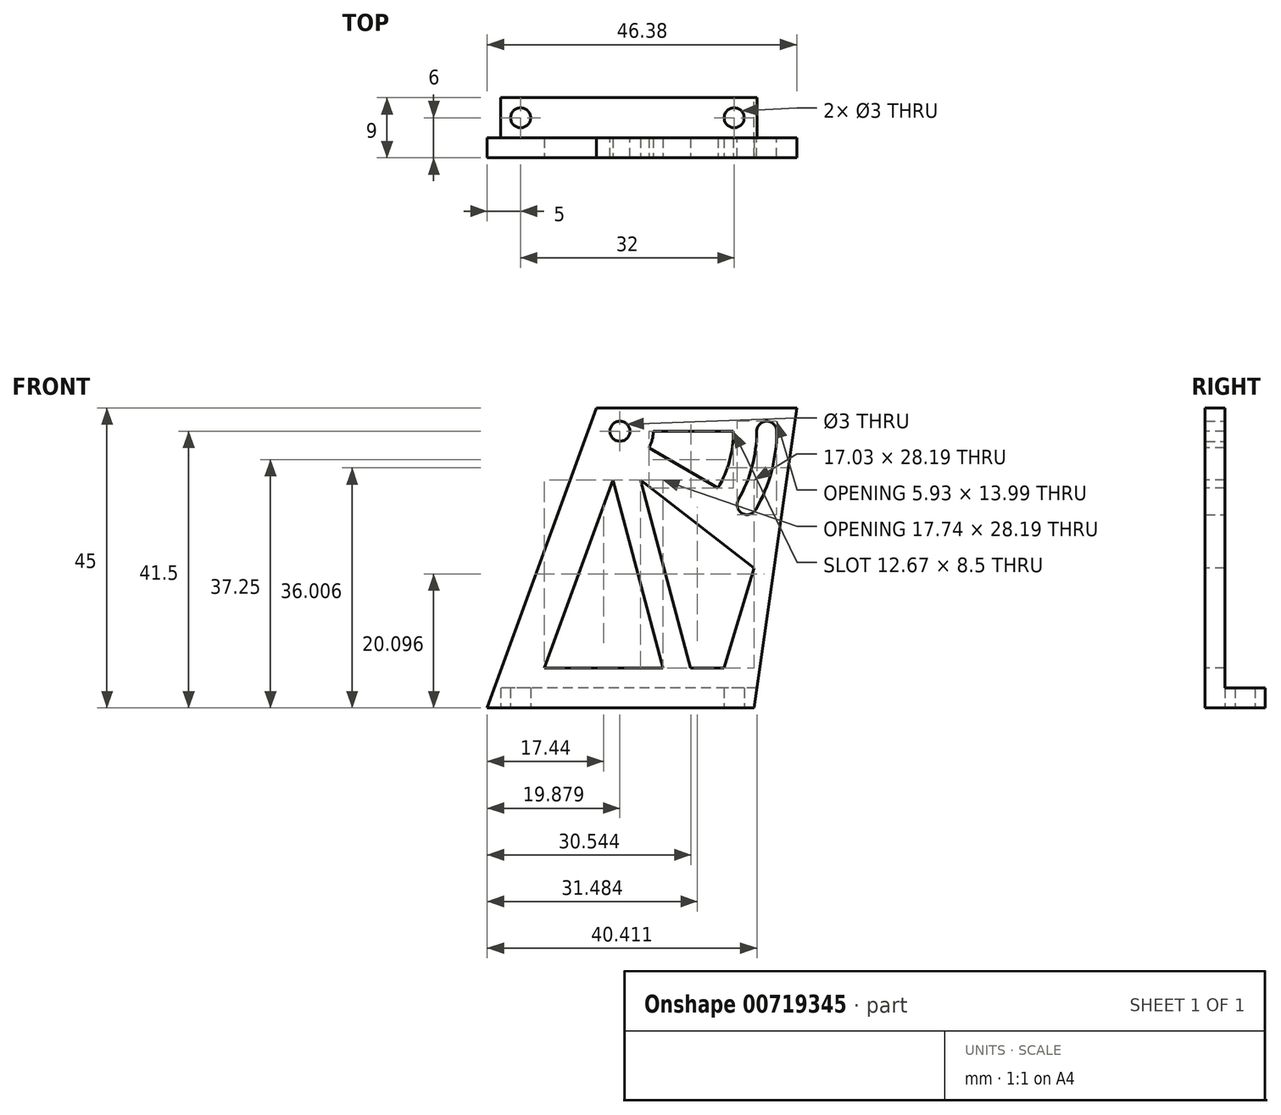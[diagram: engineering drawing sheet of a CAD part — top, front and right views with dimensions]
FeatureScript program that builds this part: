
annotation { "Feature Type Name" : "Feature", "Feature Type Description" : "" }
export const myFeature = defineFeature(function(context is Context, id is Id, definition is map)
    precondition{}
    {
        {
            var Q0;
            Q0=qCreatedBy(makeId("Front.planeOp"),FACE);
            var sketch = newSketch(context, id + "F0", { "sketchPlane" : qUnion([Q0])});
            skLineSegment(sketch, "E0", {"start": v(0, 0) * mm, "end": v(40, 0) * mm});
            skLineSegment(sketch, "E1", {"start": v(40, 0) * mm, "end": v(46.38, 45) * mm});
            skLineSegment(sketch, "E2", {"start": v(46.38, 45) * mm, "end": v(16.38, 45) * mm});
            skLineSegment(sketch, "E3", {"start": v(16.38, 45) * mm, "end": v(0, 0) * mm});
            skCircle(sketch, "E4", {"center": v(19.88, 41.5) * mm, "radius": 1.5 * mm});
            skArc(sketch, "E5", {"start": v(40.23, 29.75) * mm, "mid": v(42.58, 35.42) * mm, "end": v(43.38, 41.5) * mm});
            skArc(sketch, "E6", {"start": v(37.63, 31.25) * mm, "mid": v(39.68, 36.2) * mm, "end": v(40.38, 41.5) * mm});
            skArc(sketch, "E7", {"start": v(43.38, 41.5) * mm, "mid": v(41.88, 43) * mm, "end": v(40.38, 41.5) * mm});
            skArc(sketch, "E8", {"start": v(37.63, 31.25) * mm, "mid": v(38.18, 29.2) * mm, "end": v(40.23, 29.75) * mm});
            skSolve(sketch);
        }
        {
            var Q0;
            Q0 = qSketchRegion(id + "F0", true);
            extrude(context, id + "F1", {"entities" : qUnion([Q0]), "depth" : 3 * mm, "offsetDistance" : 25 * mm});
        }
        {
            var Q0;
            Q0=makeQuery(id+"F1.opExtrude","CAP_FACE",FACE,{"disambiguationData":[OSD([sQuery(id+"F0.wireOp",EDGE,"E0"),sQuery(id+"F0.wireOp",EDGE,"E1"),sQuery(id+"F0.wireOp",EDGE,"E2"),sQuery(id+"F0.wireOp",EDGE,"E3"),sQuery(id+"F0.wireOp",EDGE,"E4"),sQuery(id+"F0.wireOp",EDGE,"E5"),sQuery(id+"F0.wireOp",EDGE,"E6"),sQuery(id+"F0.wireOp",EDGE,"E7"),sQuery(id+"F0.wireOp",EDGE,"E8")])],"isStart":true});
            var sketch = newSketch(context, id + "F2", { "sketchPlane" : qUnion([Q0])});
            skLineSegment(sketch, "E9", {"start": v(-40, 0) * mm, "end": v(-40.43, 3) * mm});
            skLineSegment(sketch, "E10", {"start": v(-40.43, 3) * mm, "end": v(-2, 3) * mm});
            skLineSegment(sketch, "E11", {"start": v(-2, 3) * mm, "end": v(-2, 0) * mm});
            skLineSegment(sketch, "E12", {"start": v(-2, 0) * mm, "end": v(-40, 0) * mm});
            skSolve(sketch);
        }
        {
            var Q0;
            Q0 = qSketchRegion(id + "F2", true);
            extrude(context, id + "F3", {"entities" : qUnion([Q0]), "operationType" : NewBodyOperationType.ADD, "depth" : 6 * mm, "offsetDistance" : 25 * mm});
        }
        {
            var Q0;
            Q0=makeQuery(id+"F3.boolean.opBoolean","MERGE",FACE,{"derivedFrom":[makeQuery(id+"F1.opExtrude","SWEPT_FACE",FACE,{"disambiguationData":[OSD([sQuery(id+"F0.wireOp",EDGE,"E0")])]}),makeQuery(id+"F3.opExtrude","SWEPT_FACE",FACE,{"disambiguationData":[OSD([sQuery(id+"F2.wireOp",EDGE,"E12")])]})]});
            var sketch = newSketch(context, id + "F4", { "sketchPlane" : qUnion([Q0])});
            skCircle(sketch, "E13", {"center": v(37, -3) * mm, "radius": 1.5 * mm});
            skCircle(sketch, "E14", {"center": v(5, -3) * mm, "radius": 1.5 * mm});
            skSolve(sketch);
        }
        {
            var Q0;
            Q0 = qSketchRegion(id + "F4", true);
            extrude(context, id + "F5", {"entities" : qUnion([Q0]), "operationType" : NewBodyOperationType.REMOVE, "oppositeDirection" : true, "depth" : 25 * mm, "offsetDistance" : 25 * mm});
        }
        {
            var Q0;
            Q0=makeQuery(id+"F1.opExtrude","CAP_FACE",FACE,{"disambiguationData":[OSD([sQuery(id+"F0.wireOp",EDGE,"E0"),sQuery(id+"F0.wireOp",EDGE,"E1"),sQuery(id+"F0.wireOp",EDGE,"E2"),sQuery(id+"F0.wireOp",EDGE,"E3"),sQuery(id+"F0.wireOp",EDGE,"E4"),sQuery(id+"F0.wireOp",EDGE,"E5"),sQuery(id+"F0.wireOp",EDGE,"E6"),sQuery(id+"F0.wireOp",EDGE,"E7"),sQuery(id+"F0.wireOp",EDGE,"E8")])],"isStart":false});
            var sketch = newSketch(context, id + "F6", { "sketchPlane" : qUnion([Q0])});
            skLineSegment(sketch, "E15", {"start": v(8.57, 6) * mm, "end": v(18.83, 34.2) * mm});
            skLineSegment(sketch, "E16", {"start": v(18.83, 34.2) * mm, "end": v(26.31, 6) * mm});
            skLineSegment(sketch, "E17", {"start": v(26.31, 6) * mm, "end": v(8.57, 6) * mm});
            skLineSegment(sketch, "E18", {"start": v(22.97, 34.2) * mm, "end": v(30.45, 6) * mm});
            skLineSegment(sketch, "E19", {"start": v(30.45, 6) * mm, "end": v(35.45, 6) * mm});
            skLineSegment(sketch, "E20", {"start": v(35.45, 6) * mm, "end": v(40, 21) * mm});
            skLineSegment(sketch, "E21", {"start": v(40, 21) * mm, "end": v(22.97, 34.2) * mm});
            skArc(sketch, "E22", {"start": v(24.2, 39) * mm, "mid": v(24.7, 40.2) * mm, "end": v(24.88, 41.5) * mm});
            skLineSegment(sketch, "E23", {"start": v(24.88, 41.5) * mm, "end": v(36.88, 41.5) * mm});
            skLineSegment(sketch, "E24", {"start": v(24.2, 39) * mm, "end": v(34.6, 33) * mm});
            skArc(sketch, "E25.trimOffspring", {"start": v(34.6, 33) * mm, "mid": v(36.3, 37.1) * mm, "end": v(36.88, 41.5) * mm});
            skPoint(sketch, "E26.orphan", {"position": v(38.93, 30.5) * mm});
            skSolve(sketch);
        }
        {
            var Q0;
            Q0 = qSketchRegion(id + "F6", true);
            extrude(context, id + "F7", {"entities" : qUnion([Q0]), "operationType" : NewBodyOperationType.REMOVE, "oppositeDirection" : true, "depth" : 25 * mm, "offsetDistance" : 25 * mm});
        }
    });
